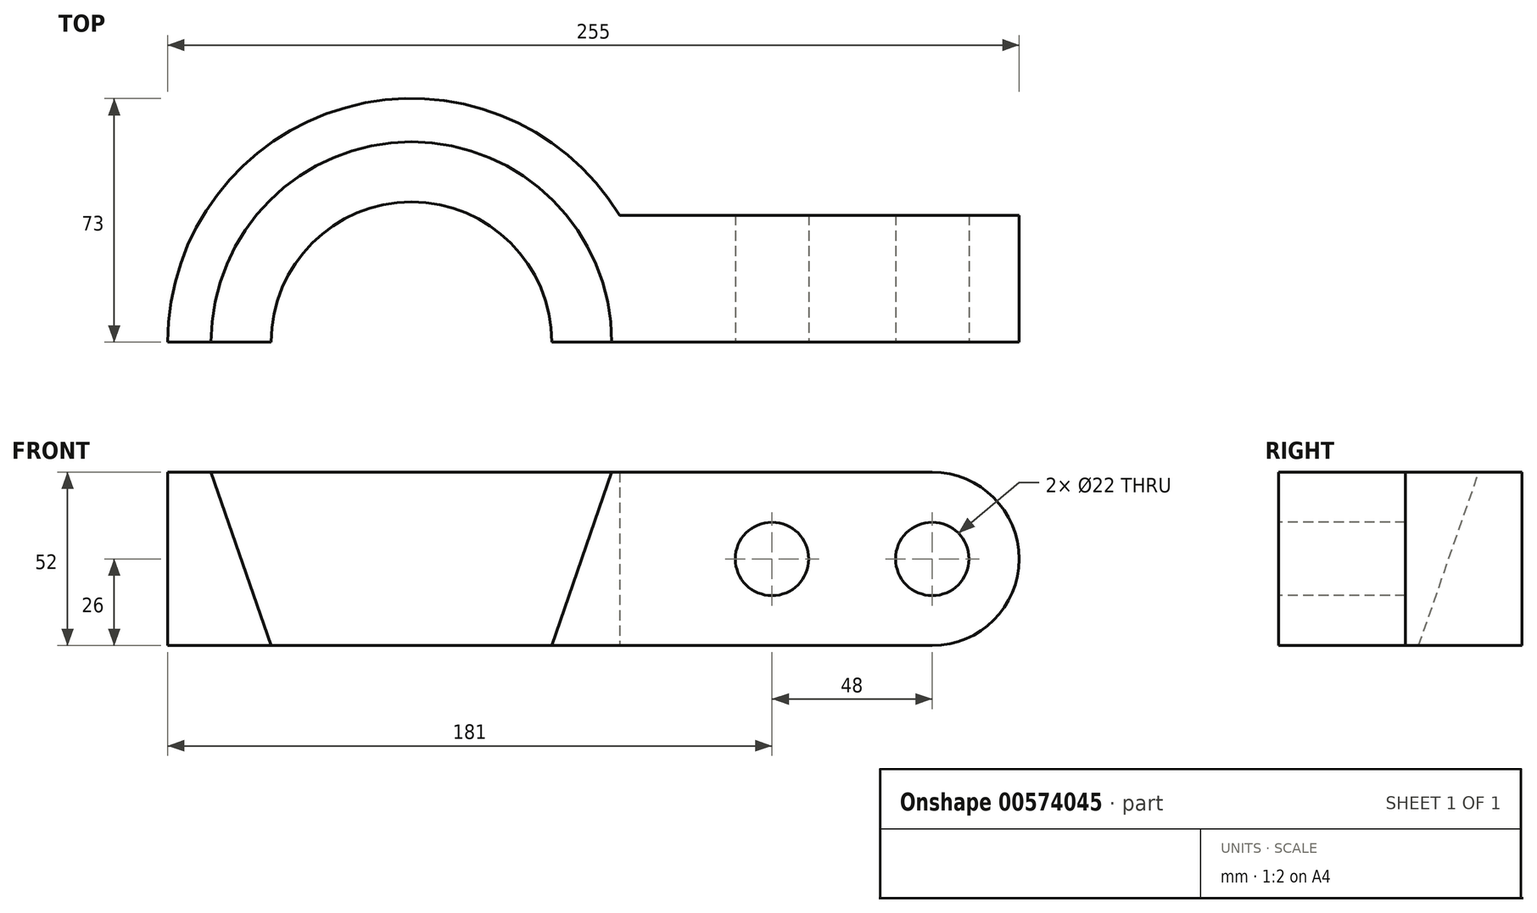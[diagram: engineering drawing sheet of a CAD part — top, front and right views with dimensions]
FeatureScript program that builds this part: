
annotation { "Feature Type Name" : "Feature", "Feature Type Description" : "" }
export const myFeature = defineFeature(function(context is Context, id is Id, definition is map)
    precondition{}
    {
        {
            var Q0;
            Q0=qCreatedBy(makeId("Top.planeOp"),FACE);
            var sketch = newSketch(context, id + "F0", { "sketchPlane" : qUnion([Q0])});
            skArc(sketch, "E0", {"start": v(62.33, 38) * mm, "mid": v(-19.73, 70.28) * mm, "end": v(-73, 0) * mm});
            skArc(sketch, "E1", {"start": v(60, 0) * mm, "mid": v(0, 60) * mm, "end": v(-60, 0) * mm});
            skArc(sketch, "E2", {"start": v(42, 0) * mm, "mid": v(0, 42) * mm, "end": v(-42, 0) * mm});
            skLineSegment(sketch, "E3", {"start": v(-73, 0) * mm, "end": v(-42, 0) * mm});
            skLineSegment(sketch, "E4", {"start": v(182, 0) * mm, "end": v(182, 38) * mm});
            skLineSegment(sketch, "E5", {"start": v(182, 38) * mm, "end": v(62.33, 38) * mm});
            skLineSegment(sketch, "E6.trimOffspring", {"start": v(42, 0) * mm, "end": v(182, 0) * mm});
            skSolve(sketch);
        }
        {
            var Q0;
            {var subQ1=sQuery(id+"F0.wireOp",EDGE,"E0");Q0=makeQuery(id+"F0.imprint","IMPRINT",FACE,{"disambiguationData":[TD([[makeQuery(id+"F0.imprint","IMPRINT",EDGE,{"derivedFrom":subQ1}),1.0]])]});}
            var Q1;
            {var subQ0=sQuery(id+"F0.wireOp",EDGE,"E1");Q1=makeQuery(id+"F0.imprint","IMPRINT",FACE,{"disambiguationData":[TD([[makeQuery(id+"F0.imprint","IMPRINT",EDGE,{"derivedFrom":subQ0}),1.0]])]});}
            extrude(context, id + "F1", {"entities" : qUnion([Q0, Q1]), "depth" : 52 * mm, "offsetDistance" : 25 * mm});
        }
        {
            var Q0;
            Q0=makeQuery(id+"F1.opExtrude","SWEPT_FACE",FACE,{"disambiguationData":[OSD([sQuery(id+"F0.wireOp",EDGE,"E3")])]});
            var sketch = newSketch(context, id + "F2", { "sketchPlane" : qUnion([Q0])});
            skLineSegment(sketch, "E7", {"start": v(-42, 0) * mm, "end": v(-60, 52) * mm});
            skLineSegment(sketch, "E8", {"start": v(-42, 0) * mm, "end": v(-42, 52) * mm});
            skLineSegment(sketch, "E9", {"start": v(-42, 52) * mm, "end": v(-60, 52) * mm});
            skLineSegment(sketch, "E10", {"start": v(0, 52) * mm, "end": v(0, 0) * mm});
            skSolve(sketch);
        }
        {
            var Q0;
            Q0=makeQuery(id+"F2.imprint","IMPRINT",FACE,{"disambiguationData":[TD([[makeQuery(id+"F2.imprint","IMPRINT",EDGE,{"derivedFrom":sQuery(id+"F2.wireOp",EDGE,"E7")}),-1.0]])]});
            var Q1;
            Q1=sQuery(id+"F2.wireOp",EDGE,"E10");
            revolve(context, id + "F3", {"operationType" : NewBodyOperationType.REMOVE, "entities" : qUnion([Q0]), "axis" : qUnion([Q1]), "revolveType" : RevolveType.FULL, "oppositeDirection" : true});
        }
        {
            var Q0;
            Q0=makeQuery(id+"F1.opExtrude","SWEPT_FACE",FACE,{"disambiguationData":[OSD([sQuery(id+"F0.wireOp",EDGE,"E6.trimOffspring")])]});
            var sketch = newSketch(context, id + "F4", { "sketchPlane" : qUnion([Q0])});
            skCircle(sketch, "E11", {"center": v(108, 26) * mm, "radius": 11 * mm});
            skCircle(sketch, "E12", {"center": v(156, 26) * mm, "radius": 11 * mm});
            skSolve(sketch);
        }
        {
            var Q0;
            Q0=makeQuery(id+"F4.imprint","IMPRINT",FACE,{"disambiguationData":[TD([[makeQuery(id+"F4.imprint","IMPRINT",EDGE,{"derivedFrom":sQuery(id+"F4.wireOp",EDGE,"E11")}),1.0]])]});
            var Q1;
            Q1=makeQuery(id+"F4.imprint","IMPRINT",FACE,{"disambiguationData":[TD([[makeQuery(id+"F4.imprint","IMPRINT",EDGE,{"derivedFrom":sQuery(id+"F4.wireOp",EDGE,"E12")}),1.0]])]});
            extrude(context, id + "F5", {"entities" : qUnion([Q0, Q1]), "operationType" : NewBodyOperationType.REMOVE, "endBound" : BoundingType.THROUGH_ALL, "oppositeDirection" : true, "depth" : 25 * mm, "offsetDistance" : 25 * mm});
        }
        {
            var Q0;
            Q0=makeQuery(id+"F1.opExtrude","CAP_EDGE",EDGE,{"disambiguationData":[OSD([sQuery(id+"F0.wireOp",EDGE,"E4")])],"isStart":false});
            var Q1;
            Q1=makeQuery(id+"F1.opExtrude","CAP_EDGE",EDGE,{"disambiguationData":[OSD([sQuery(id+"F0.wireOp",EDGE,"E4")])],"isStart":true});
            fillet(context, id + "F6", {"entities" : qUnion([Q0, Q1]), "radius" : 26 * mm, "tangentPropagation" : true, "allowEdgeOverflow" : false});
        }
    });
